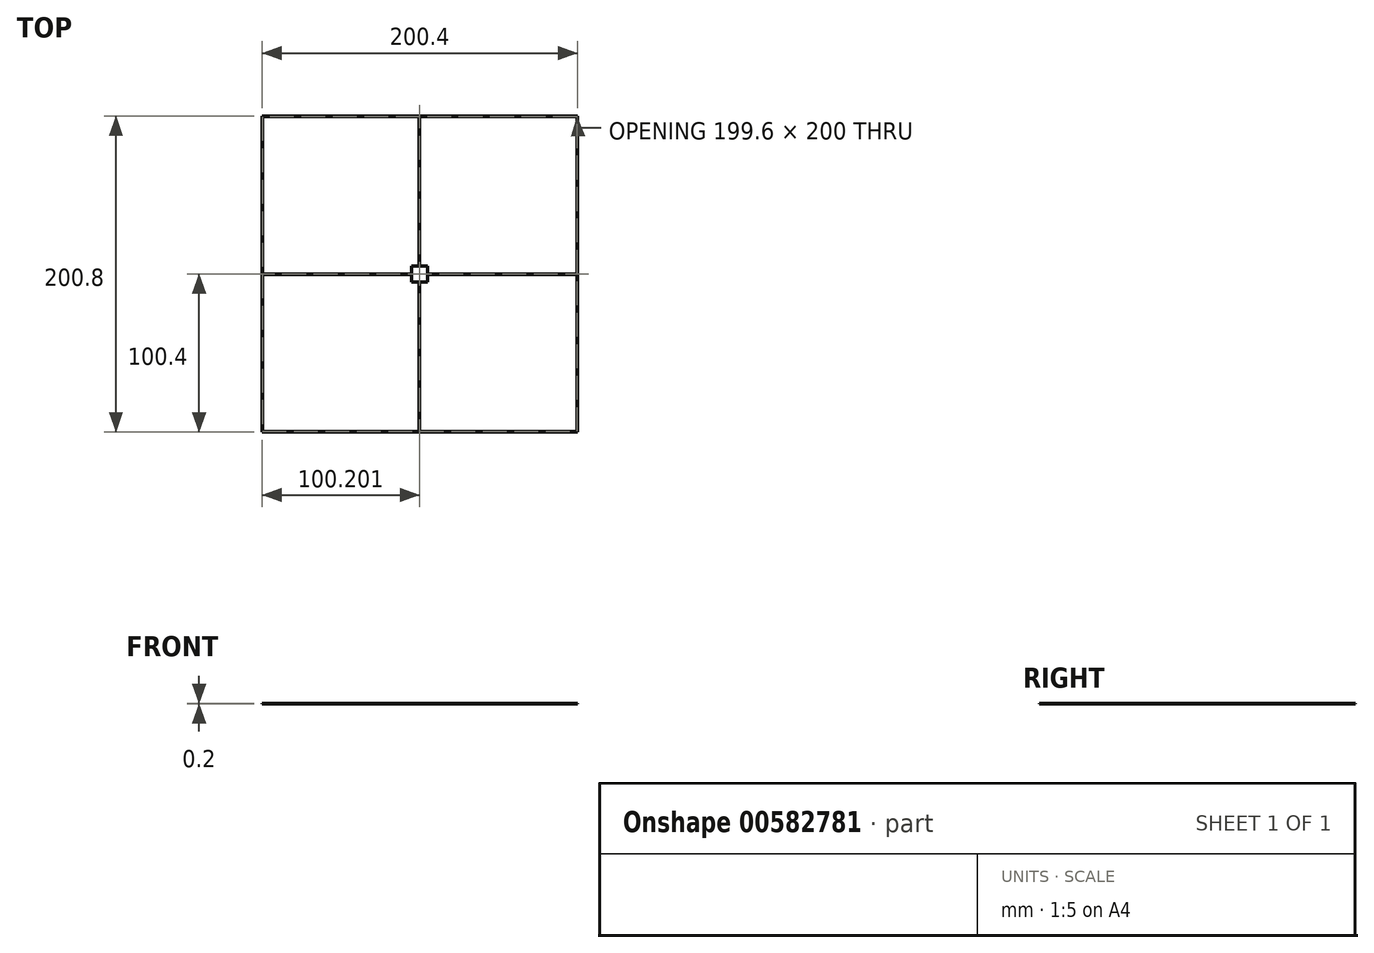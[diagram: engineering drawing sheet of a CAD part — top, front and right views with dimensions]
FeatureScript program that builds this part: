
annotation { "Feature Type Name" : "Feature", "Feature Type Description" : "" }
export const myFeature = defineFeature(function(context is Context, id is Id, definition is map)
    precondition{}
    {
        {
            var Q0;
            Q0=qCreatedBy(makeId("Top.planeOp"),FACE);
            var sketch = newSketch(context, id + "F0", { "sketchPlane" : qUnion([Q0])});
            skLineSegment(sketch, "E0.bottom", {"start": v(100, -100) * mm, "end": v(0, -100) * mm});
            skLineSegment(sketch, "E0.top", {"start": v(100, 100) * mm, "end": v(0, 100) * mm});
            skLineSegment(sketch, "E0.left", {"start": v(100, -100) * mm, "end": v(100, -0.4) * mm});
            skPoint(sketch, "E0.middle", {"position": v(0, 0) * mm});
            skLineSegment(sketch, "E1", {"start": v(-99.6, 0) * mm, "end": v(-5, 0) * mm});
            skLineSegment(sketch, "E2", {"start": v(0, 100) * mm, "end": v(0, 5) * mm});
            skLineSegment(sketch, "E3.bottom", {"start": v(5, -5) * mm, "end": v(-5, -5) * mm});
            skLineSegment(sketch, "E3.top", {"start": v(5, 5) * mm, "end": v(-5, 5) * mm});
            skLineSegment(sketch, "E3.left", {"start": v(5, -5) * mm, "end": v(5, 5) * mm});
            skLineSegment(sketch, "E3.right", {"start": v(-5, -5) * mm, "end": v(-5, 5) * mm});
            skLineSegment(sketch, "E4.trimOffspring", {"start": v(5, 0) * mm, "end": v(100, 0) * mm});
            skLineSegment(sketch, "E5.trimOffspring", {"start": v(0, -5) * mm, "end": v(0, -100) * mm});
            skLineSegment(sketch, "E6.0", {"start": v(100.4, 100.4) * mm, "end": v(-100, 100.4) * mm});
            skLineSegment(sketch, "E6.1", {"start": v(100.4, -100.4) * mm, "end": v(100.4, 100.4) * mm});
            skLineSegment(sketch, "E6.2", {"start": v(100.4, -100.4) * mm, "end": v(-100, -100.4) * mm});
            skLineSegment(sketch, "E6.3", {"start": v(-100, -100.4) * mm, "end": v(-100, 100.4) * mm});
            skLineSegment(sketch, "E7.0", {"start": v(-0.4, 100) * mm, "end": v(-0.4, 5) * mm});
            skLineSegment(sketch, "E8.0", {"start": v(-99.6, -0.4) * mm, "end": v(-5, -0.4) * mm});
            skLineSegment(sketch, "E9.0", {"start": v(-0.4, -5) * mm, "end": v(-0.4, -100) * mm});
            skLineSegment(sketch, "E10.0", {"start": v(5, -0.4) * mm, "end": v(100, -0.4) * mm});
            skLineSegment(sketch, "E11.0", {"start": v(-99.6, -100) * mm, "end": v(-99.6, -0.4) * mm});
            skPoint(sketch, "E12.orphan", {"position": v(-100, 0) * mm});
            skLineSegment(sketch, "E13.trimOffspring", {"start": v(-0.4, -100) * mm, "end": v(-100, -100) * mm});
            skLineSegment(sketch, "E14.trimOffspring", {"start": v(100, 0) * mm, "end": v(100, 100) * mm});
            skLineSegment(sketch, "E15.trimOffspring", {"start": v(-0.4, 100) * mm, "end": v(-99.6, 100) * mm});
            skLineSegment(sketch, "E16.trimOffspring", {"start": v(-100, 100) * mm, "end": v(-100, 100) * mm});
            skLineSegment(sketch, "E17.trimOffspring", {"start": v(-99.6, 0) * mm, "end": v(-99.6, 100) * mm});
            skSolve(sketch);
        }
        {
            var Q0;
            Q0=makeQuery(id+"F0.imprint","IMPRINT",FACE,{"disambiguationData":[TD([[makeQuery(id+"F0.imprint","IMPRINT",EDGE,{"derivedFrom":sQuery(id+"F0.wireOp",EDGE,"E0.bottom")}),1.0]])]});
            var Q1;
            Q1=sQuery(id+"F0.wireOp",EDGE,"E6.2");
            var Q2;
            Q2=sQuery(id+"F0.wireOp",EDGE,"E6.3");
            var Q3;
            Q3=sQuery(id+"F0.wireOp",EDGE,"E6.0");
            var Q4;
            Q4=sQuery(id+"F0.wireOp",EDGE,"E6.1");
            var Q5;
            Q5=sQuery(id+"F0.wireOp",EDGE,"E10.0");
            var Q6;
            Q6=sQuery(id+"F0.wireOp",EDGE,"E9.0");
            var Q7;
            Q7=sQuery(id+"F0.wireOp",EDGE,"E8.0");
            var Q8;
            Q8=sQuery(id+"F0.wireOp",EDGE,"E2");
            extrude(context, id + "F1", {"entities" : qUnion([Q0]), "surfaceEntities" : qUnion([Q1, Q2, Q3, Q4, Q5, Q6, Q7, Q8]), "depth" : 0.2 * mm, "offsetDistance" : 25 * mm});
        }
        {
            var Q0;
            {var subQ4=sQuery(id+"F0.wireOp",EDGE,"E3.left");var subQ6=sQuery(id+"F0.wireOp",EDGE,"E3.bottom");var subQ9=makeQuery(id+"F0.imprint","INTERSECT",VERTEX,{"derivedFrom":[subQ6,subQ4]});Q0=makeQuery(id+"F0.imprint","IMPRINT",FACE,{"disambiguationData":[TD([[makeQuery(id+"F0.imprint","IMPRINT",EDGE,{"disambiguationData":[TD([[subQ9,-1.0]])],"derivedFrom":subQ6}),-1.0]])]});}
            extrude(context, id + "F2", {"entities" : qUnion([Q0]), "depth" : .2 * mm, "offsetDistance" : 25 * mm});
        }
    });
